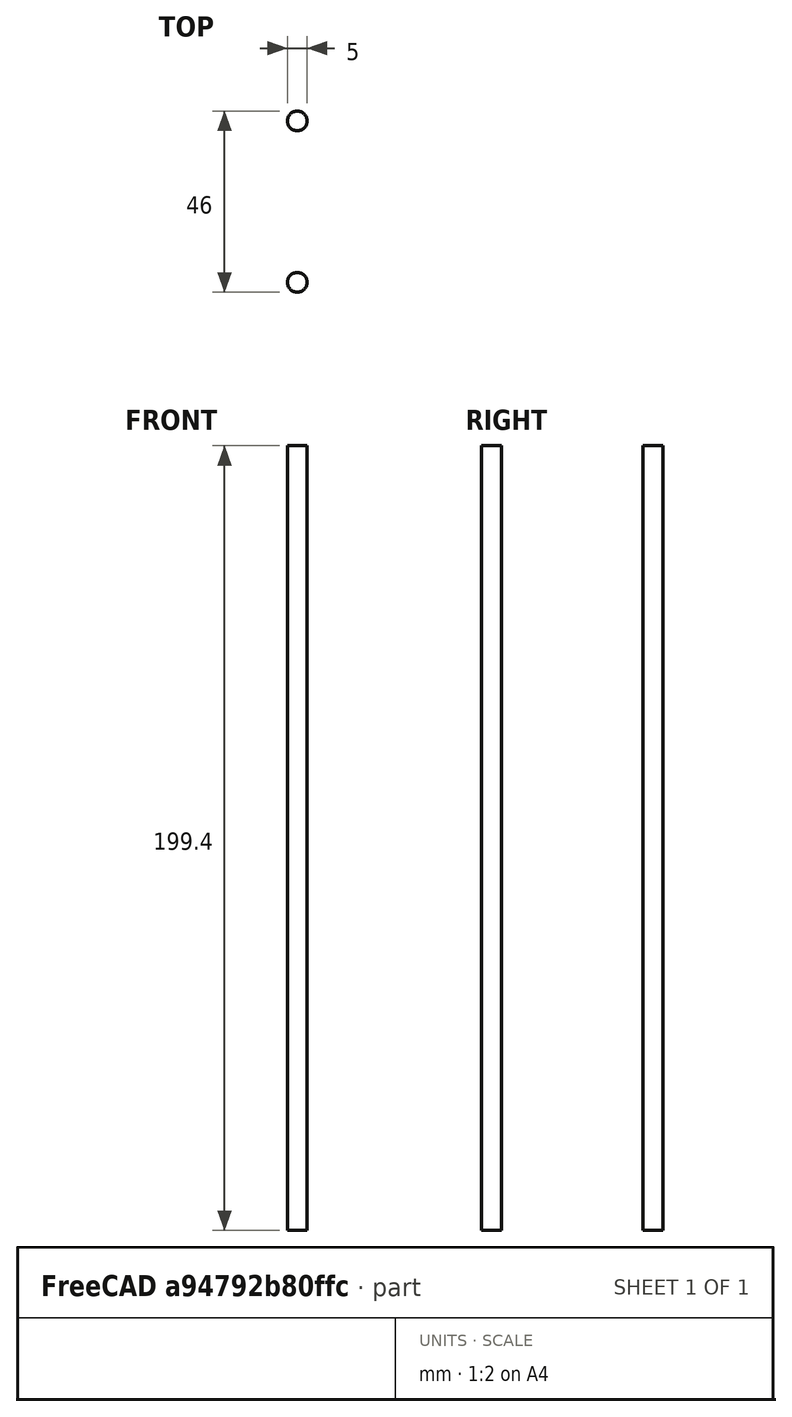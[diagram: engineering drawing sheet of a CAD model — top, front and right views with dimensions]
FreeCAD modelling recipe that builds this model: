
FCSTD DOCUMENT  (FreeCAD 1.0R39109 (Git))
Label: Stator_CoilWinder_Pins_Quadrilateral
License: All rights reserved
LicenseURL: http://en.wikipedia.org/wiki/All_rights_reserved
objects: PartDesign::SubShapeBinder×1, Part::Extrusion×1, Part::Mirroring×1, App::Part×1, Spreadsheet::Sheet×1
note: 3 computed .brp shape members not serialized (recipe doc carries the construction recipe); baked Part::Feature solids carry a one-line shape summary decoded from their .brp
EXTERNAL_REF file=Stator_CoilWinder_Cheek.FCStd obj=PolarPattern001Body
EXTERNAL_REF file=../../../Master_of_Puppets.FCStd obj=Alternator

FEATURE [PartDesign::SubShapeBinder] Binder  label="PinHolesSketchBinder"
  BindCopyOnChange = 0
  BindMode = 0
  ClaimChildren = false
  Context = -> Part [Binder.]
  Fuse = false
  MakeFace = true
  OffsetFill = false
  OffsetIntersection = false
  OffsetJoinType = 0
  OffsetOpenResult = false
  PartialLoad = false
  Relative = true
  Support = -> [<external Stator_CoilWinder_Cheek.FCStd>#PolarPattern001Body[Sketch002.]]
  _Version = 2
FEATURE [Part::Extrusion] Extrude
  Base = -> Binder
  Dir = (0,0,1)
  DirMode = 2
  FaceMakerClass = Part::FaceMakerBullseye
  FaceMakerMode = 3
  LengthFwd = 199.4
  LengthRev = 0
  Solid = false
  Symmetric = false
  expr: LengthFwd = Spreadsheet.CoilWinderPinLength
FEATURE [Part::Mirroring] Part__Mirroring  label="Mirror"
  Base = (0,0,0)
  Normal = (1,0,0)
  Source = -> Extrude
FEATURE [App::Part] Part  label="Stator_CoilWinder_Pins"
  Group = -> [Extrude,Binder,Part__Mirroring]
  Origin = -> Origin
FEATURE [Spreadsheet::Sheet] Spreadsheet
  cells = A1='Inputs; A2='CoilWinderPinLength; B2(CoilWinderPinLength)==Master_of_Puppets#Alternator.CoilWinderPinLength
